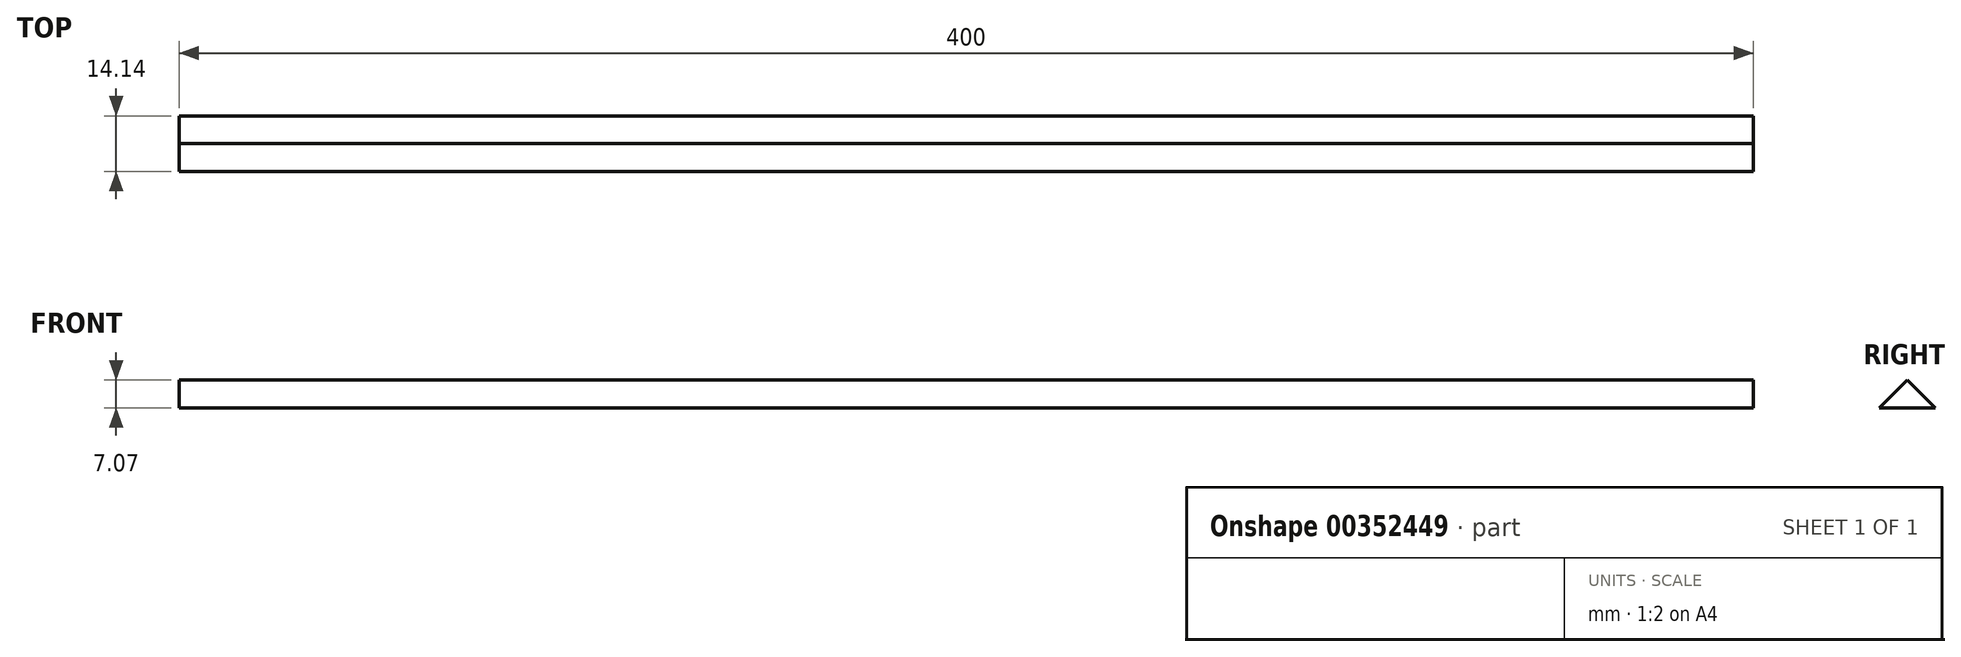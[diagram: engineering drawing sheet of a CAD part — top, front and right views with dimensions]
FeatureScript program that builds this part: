
annotation { "Feature Type Name" : "Feature", "Feature Type Description" : "" }
export const myFeature = defineFeature(function(context is Context, id is Id, definition is map)
    precondition{}
    {
        {
            var Q0;
            Q0=qCreatedBy(makeId("Right.planeOp"),FACE);
            var sketch = newSketch(context, id + "F0", { "sketchPlane" : qUnion([Q0])});
            skLineSegment(sketch, "E0", {"start": v(-7.07, 0) * mm, "end": v(7.07, 0) * mm});
            skLineSegment(sketch, "E1", {"start": v(0, 7.07) * mm, "end": v(-7.07, 0) * mm});
            skLineSegment(sketch, "E2.MirrorCS", {"start": v(0, 7.07) * mm, "end": v(7.07, 0) * mm});
            skSolve(sketch);
        }
        {
            var Q0;
            Q0 = qSketchRegion(id + "F0", true);
            extrude(context, id + "F1", {"entities" : qUnion([Q0]), "depth" : 400 * mm, "symmetric" : true});
        }
    });
